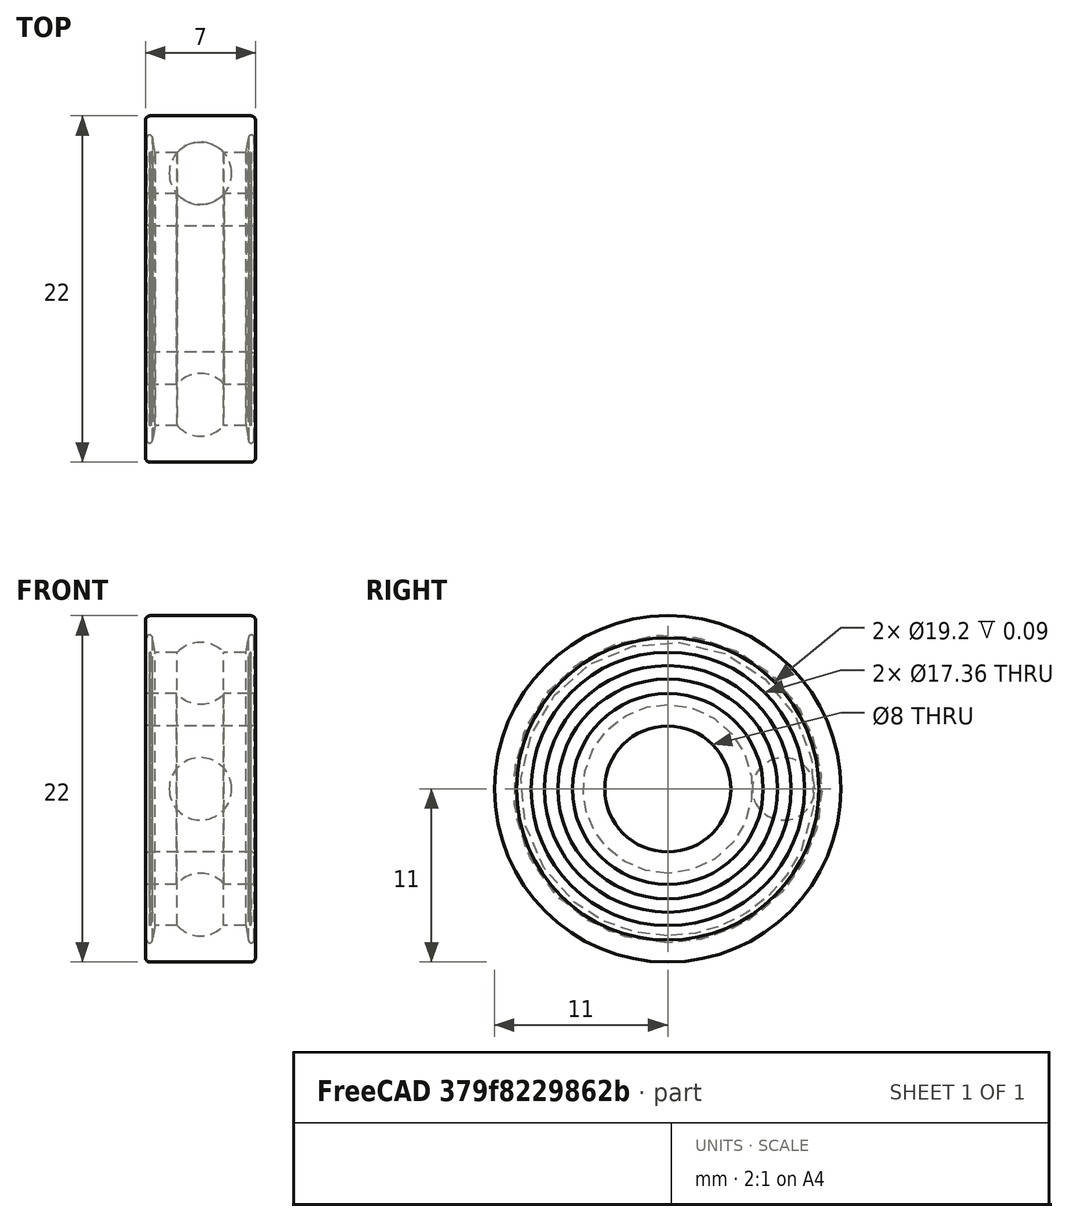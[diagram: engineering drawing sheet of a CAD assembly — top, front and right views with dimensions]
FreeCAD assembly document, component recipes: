
FREECAD ASSEMBLY — COMPONENT RECIPES ("lozysko 608")

This assembly document has 6 components, labeled P0..P5 below (a component is one placed body or linked part). 0 of them carry a construction recipe — the FreeCAD feature program that regenerates the part from scratch, quoted from this document or its linked companion documents; the rest are supplied as boundary geometry only. No exploded tour is included for this assembly.
COMPONENT P0 — geometry summary ("_608-2RSH_PART004"; no construction recipe available for this part):
  bounding box: 4.0 x 4.0 x 4.0 mm
  tessellated surface: 8,014 triangles
  volume: 33 mm^3 (52% of its bounding box)
  symmetry: revolution-symmetric about the x axis through its bounding-box center; revolution-symmetric about the y axis through its bounding-box center; revolution-symmetric about the z axis through its bounding-box center; mirror-symmetric across its x mid-plane, y mid-plane, z mid-plane
COMPONENT P1 — geometry summary ("_608-2RSH_PART005"; no construction recipe available for this part):
  bounding box: 4.0 x 4.0 x 4.0 mm
  tessellated surface: 8,014 triangles
  volume: 33 mm^3 (52% of its bounding box)
  symmetry: revolution-symmetric about the x axis through its bounding-box center; revolution-symmetric about the y axis through its bounding-box center; revolution-symmetric about the z axis through its bounding-box center; mirror-symmetric across its x mid-plane, y mid-plane, z mid-plane
COMPONENT P2 — geometry summary ("_608-2RSH_PART006"; no construction recipe available for this part):
  bounding box: 4.0 x 4.0 x 4.0 mm
  tessellated surface: 8,014 triangles
  volume: 33 mm^3 (52% of its bounding box)
  symmetry: revolution-symmetric about the x axis through its bounding-box center; revolution-symmetric about the y axis through its bounding-box center; revolution-symmetric about the z axis through its bounding-box center; mirror-symmetric across its x mid-plane, y mid-plane, z mid-plane
COMPONENT P3 — geometry summary ("_608-2RSH_PART007"; no construction recipe available for this part):
  bounding box: 4.0 x 4.0 x 4.0 mm
  tessellated surface: 8,014 triangles
  volume: 33 mm^3 (52% of its bounding box)
  symmetry: revolution-symmetric about the x axis through its bounding-box center; revolution-symmetric about the y axis through its bounding-box center; revolution-symmetric about the z axis through its bounding-box center; mirror-symmetric across its x mid-plane, y mid-plane, z mid-plane
COMPONENT P4 — geometry summary ("_608-2RSH_PART008"; no construction recipe available for this part):
  bounding box: 4.0 x 4.0 x 4.0 mm
  tessellated surface: 8,014 triangles
  volume: 33 mm^3 (52% of its bounding box)
  symmetry: revolution-symmetric about the x axis through its bounding-box center; revolution-symmetric about the y axis through its bounding-box center; revolution-symmetric about the z axis through its bounding-box center; mirror-symmetric across its x mid-plane, y mid-plane, z mid-plane
COMPONENT P5 — geometry summary ("_608-2RSH_PART009"; no construction recipe available for this part):
  bounding box: 4.0 x 4.0 x 4.0 mm
  tessellated surface: 8,014 triangles
  volume: 33 mm^3 (52% of its bounding box)
  symmetry: revolution-symmetric about the x axis through its bounding-box center; revolution-symmetric about the y axis through its bounding-box center; revolution-symmetric about the z axis through its bounding-box center; mirror-symmetric across its x mid-plane, y mid-plane, z mid-plane
PROVENANCE & LICENSES
A FreeCAD (.FCStd) document from a public repository crawl; recipes are the document's own serialized feature recipes (and, for linked parts, companion documents' recipes).
License: bsd.
